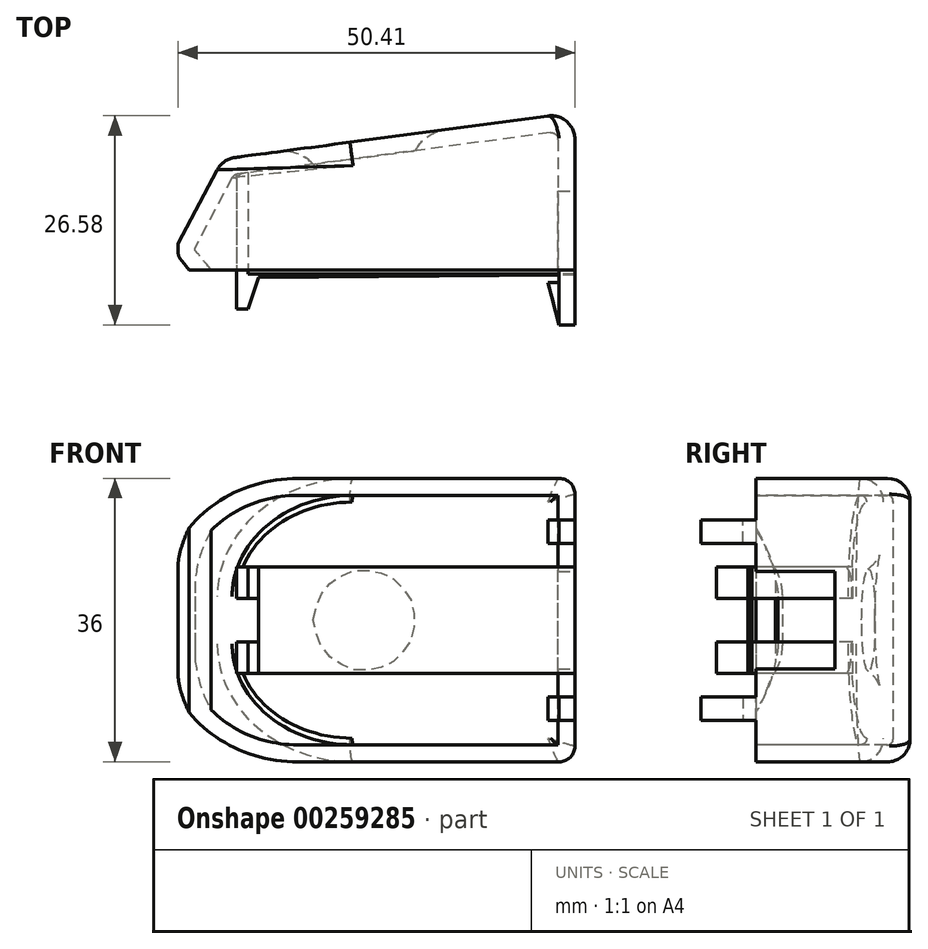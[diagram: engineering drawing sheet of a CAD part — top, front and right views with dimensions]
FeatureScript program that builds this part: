
annotation { "Feature Type Name" : "Feature", "Feature Type Description" : "" }
export const myFeature = defineFeature(function(context is Context, id is Id, definition is map)
    precondition{}
    {
        {
            var Q0;
            Q0=qCreatedBy(makeId("Top.planeOp"),FACE);
            var sketch = newSketch(context, id + "F0", { "sketchPlane" : qUnion([Q0])});
            skLineSegment(sketch, "E0.bottom", {"start": v(24.5, -10) * mm, "end": v(-24.5, -10) * mm});
            skLineSegment(sketch, "E0.left", {"start": v(24.5, -10) * mm, "end": v(24.5, 10) * mm});
            skPoint(sketch, "E0.middle", {"position": v(0, 0) * mm});
            skLineSegment(sketch, "E1", {"start": v(-20.22, 4.07) * mm, "end": v(24.5, 10) * mm});
            skLineSegment(sketch, "E2", {"start": v(-24.5, -10) * mm, "end": v(-25.9, -8.28) * mm});
            skLineSegment(sketch, "E3", {"start": v(-25.9, -8.28) * mm, "end": v(-25.9, -6.67) * mm});
            skLineSegment(sketch, "E4", {"start": v(-25.9, -6.67) * mm, "end": v(-20.22, 4.07) * mm});
            skSolve(sketch);
        }
        {
            var Q0;
            Q0=makeQuery(id+"F0.imprint","IMPRINT",FACE,{"disambiguationData":[TD([[makeQuery(id+"F0.imprint","IMPRINT",EDGE,{"derivedFrom":sQuery(id+"F0.wireOp",EDGE,"E0.bottom")}),-1.0]])]});
            var sketch = newSketch(context, id + "F1", { "sketchPlane" : qUnion([Q0])});
            skSolve(sketch);
        }
        {
            var Q0;
            Q0 = qSketchRegion(id + "F1", true);
            var Q1;
            Q1=makeQuery(id+"F0.imprint","IMPRINT",FACE,{"disambiguationData":[TD([[makeQuery(id+"F0.imprint","IMPRINT",EDGE,{"derivedFrom":sQuery(id+"F0.wireOp",EDGE,"E0.bottom")}),-1.0]])]});
            extrude(context, id + "F2", {"entities" : qUnion([Q0, Q1]), "depth" : 36 * mm});
        }
        {
            var Q0;
            Q0=makeQuery(id+"F2.opExtrude","CAP_EDGE",EDGE,{"disambiguationData":[OSD([sQuery(id+"F0.wireOp",EDGE,"E4")])],"isStart":false});
            var Q1;
            Q1=makeQuery(id+"F2.opExtrude","CAP_EDGE",EDGE,{"disambiguationData":[OSD([sQuery(id+"F0.wireOp",EDGE,"E4")])],"isStart":true});
            fillet(context, id + "F3", {"entities" : qUnion([Q0, Q1]), "radius" : 15 * mm, "tangentPropagation" : true, "allowEdgeOverflow" : false});
        }
        {
            var Q0;
            Q0=makeQuery(id+"F2.opExtrude","SWEPT_FACE",FACE,{"disambiguationData":[OSD([sQuery(id+"F0.wireOp",EDGE,"E1")])]});
            fillet(context, id + "F4", {"entities" : qUnion([Q0]), "radius" : 3 * mm, "tangentPropagation" : true, "allowEdgeOverflow" : false});
        }
        {
            var Q0;
            Q0=makeQuery(id+"F2.opExtrude","CAP_EDGE",EDGE,{"disambiguationData":[OSD([sQuery(id+"F0.wireOp",EDGE,"E0.left")])],"isStart":false});
            var Q1;
            Q1=makeQuery(id+"F2.opExtrude","CAP_EDGE",EDGE,{"disambiguationData":[OSD([sQuery(id+"F0.wireOp",EDGE,"E0.left")])],"isStart":true});
            fillet(context, id + "F5", {"entities" : qUnion([Q0, Q1]), "radius" : 2 * mm, "tangentPropagation" : true, "allowEdgeOverflow" : false});
        }
        {
            var Q0;
            Q0=makeQuery(id+"F2.opExtrude","SWEPT_FACE",FACE,{"disambiguationData":[OSD([sQuery(id+"F0.wireOp",EDGE,"E0.bottom")])]});
            var sketch = newSketch(context, id + "F6", { "sketchPlane" : qUnion([Q0])});
            skLineSegment(sketch, "E5", {"start": v(24.5, 30.74) * mm, "end": v(24.5, 27.74) * mm});
            skLineSegment(sketch, "E6.0", {"start": v(-17, 24.75) * mm, "end": v(-17, 20.75) * mm});
            skLineSegment(sketch, "E7.0", {"start": v(-18.5, 11.25) * mm, "end": v(-17, 11.25) * mm});
            skLineSegment(sketch, "E8.0", {"start": v(-18.5, 15.25) * mm, "end": v(-17, 15.25) * mm});
            skPoint(sketch, "E9.orphan", {"position": v(-17, 2) * mm});
            skPoint(sketch, "E10.orphan", {"position": v(-18.5, 2) * mm});
            skLineSegment(sketch, "E11", {"start": v(-18.5, 15.25) * mm, "end": v(-18.5, 11.25) * mm});
            skLineSegment(sketch, "E12.trimOffspring", {"start": v(-17, 15.25) * mm, "end": v(-17, 11.25) * mm});
            skLineSegment(sketch, "E13.MirrorCS", {"start": v(-18.5, 20.75) * mm, "end": v(-17, 20.75) * mm});
            skLineSegment(sketch, "E14.MirrorCS", {"start": v(-18.5, 20.75) * mm, "end": v(-18.5, 24.75) * mm});
            skLineSegment(sketch, "E15.MirrorCS", {"start": v(-18.5, 24.75) * mm, "end": v(-17, 24.75) * mm});
            skPoint(sketch, "E16.orphan", {"position": v(-17, 34) * mm});
            skLineSegment(sketch, "E17", {"start": v(22.5, 36) * mm, "end": v(31.56, 36) * mm, "construction": true});
            skLineSegment(sketch, "E18.0", {"start": v(22.5, 30.74) * mm, "end": v(24.5, 30.74) * mm});
            skLineSegment(sketch, "E19.0", {"start": v(22.5, 27.74) * mm, "end": v(24.5, 27.74) * mm});
            skLineSegment(sketch, "E20.0", {"start": v(22.5, 30.74) * mm, "end": v(22.5, 27.74) * mm});
            skLineSegment(sketch, "E21", {"start": v(24.5, 18) * mm, "end": v(40.76, 18) * mm, "construction": true});
            skLineSegment(sketch, "E22.MirrorCS", {"start": v(22.5, 8.26) * mm, "end": v(24.5, 8.26) * mm});
            skLineSegment(sketch, "E23.MirrorCS", {"start": v(22.5, 5.26) * mm, "end": v(24.5, 5.26) * mm});
            skLineSegment(sketch, "E24.MirrorCS", {"start": v(22.5, 5.26) * mm, "end": v(22.5, 8.26) * mm});
            skLineSegment(sketch, "E25.trimOffspring", {"start": v(24.5, 8.26) * mm, "end": v(24.5, 5.26) * mm});
            skPoint(sketch, "E26.orphan", {"position": v(24.5, 34) * mm});
            skPoint(sketch, "E27.orphan", {"position": v(24.5, 2) * mm});
            skLineSegment(sketch, "E28", {"start": v(24.5, 18) * mm, "end": v(-2.25, 18) * mm, "construction": true});
            skCircle(sketch, "E29", {"center": v(-2.25, 18) * mm, "radius": 6.5 * mm});
            skSolve(sketch);
        }
        {
            var Q0;
            Q0=makeQuery(id+"F2.opExtrude","SWEPT_FACE",FACE,{"disambiguationData":[OSD([sQuery(id+"F0.wireOp",EDGE,"E0.bottom")])]});
            shell(context, id + "F7", {"entities" : qUnion([Q0]), "thickness" : 2.15 * mm});
        }
        {
            var Q0;
            Q0=makeQuery(id+"F6.imprint","IMPRINT",FACE,{"disambiguationData":[TD([[makeQuery(id+"F6.imprint","IMPRINT",EDGE,{"derivedFrom":sQuery(id+"F6.wireOp",EDGE,"E5")}),-1.0]])]});
            var Q1;
            Q1=makeQuery(id+"F6.imprint","IMPRINT",FACE,{"disambiguationData":[TD([[makeQuery(id+"F6.imprint","IMPRINT",EDGE,{"derivedFrom":sQuery(id+"F6.wireOp",EDGE,"E22.MirrorCS")}),-1.0]])]});
            extrude(context, id + "F8", {"entities" : qUnion([Q0, Q1]), "operationType" : NewBodyOperationType.ADD, "depth" : 7 * mm});
        }
        {
            var Q0;
            Q0=makeQuery(id+"F6.imprint","IMPRINT",FACE,{"disambiguationData":[TD([[makeQuery(id+"F6.imprint","IMPRINT",EDGE,{"derivedFrom":sQuery(id+"F6.wireOp",EDGE,"E6.0")}),-1.0]])]});
            var Q1;
            Q1=makeQuery(id+"F6.imprint","IMPRINT",FACE,{"disambiguationData":[TD([[makeQuery(id+"F6.imprint","IMPRINT",EDGE,{"derivedFrom":sQuery(id+"F6.wireOp",EDGE,"E7.0")}),1.0]])]});
            extrude(context, id + "F9", {"entities" : qUnion([Q0, Q1]), "operationType" : NewBodyOperationType.ADD, "oppositeDirection" : true, "depth" : 14.2 * mm});
        }
        {
            var Q0;
            Q0=makeQuery(id+"F2.opExtrude","SWEPT_EDGE",EDGE,{"disambiguationData":[OSD([sQuery(id+"F0.wireOp",EDGE,"E2"),sQuery(id+"F0.wireOp",EDGE,"E3")])]});
            fillet(context, id + "F10", {"entities" : qUnion([Q0]), "radius" : 1.62 * mm, "tangentPropagation" : true, "allowEdgeOverflow" : false});
        }
        {
            var Q0;
            Q0=makeQuery(id+"F6.imprint","IMPRINT",FACE,{"disambiguationData":[TD([[makeQuery(id+"F6.imprint","IMPRINT",EDGE,{"derivedFrom":sQuery(id+"F6.wireOp",EDGE,"E6.0")}),-1.0]])]});
            var Q1;
            Q1=makeQuery(id+"F6.imprint","IMPRINT",FACE,{"disambiguationData":[TD([[makeQuery(id+"F6.imprint","IMPRINT",EDGE,{"derivedFrom":sQuery(id+"F6.wireOp",EDGE,"E7.0")}),1.0]])]});
            extrude(context, id + "F11", {"entities" : qUnion([Q0, Q1]), "operationType" : NewBodyOperationType.ADD, "depth" : 5 * mm});
        }
        {
            var Q0;
            Q0=makeQuery(id+"F6.imprint","IMPRINT",FACE,{"disambiguationData":[TD([[makeQuery(id+"F6.imprint","IMPRINT",EDGE,{"derivedFrom":sQuery(id+"F6.wireOp",EDGE,"E29")}),1.0]])]});
            extrude(context, id + "F12", {"entities" : qUnion([Q0]), "operationType" : NewBodyOperationType.REMOVE, "oppositeDirection" : true, "depth" : 25 * mm});
        }
        {
            var Q0;
            Q0=makeQuery(id+"F12.boolean.opBoolean","INTERSECT",EDGE,{"derivedFrom":[makeQuery(id+"F2.opExtrude","SWEPT_FACE",FACE,{"disambiguationData":[OSD([sQuery(id+"F0.wireOp",EDGE,"E1")])]}),makeQuery(id+"F12.opExtrude","SWEPT_FACE",FACE,{"disambiguationData":[OSD([sQuery(id+"F6.wireOp",EDGE,"E29")])]})]});
            fillet(context, id + "F13", {"entities" : qUnion([Q0]), "radius" : 5 * mm, "tangentPropagation" : true, "allowEdgeOverflow" : false});
        }
        {
            var Q0;
            Q0=makeQuery(id+"F8.opExtrude","SWEPT_FACE",FACE,{"disambiguationData":[OSD([sQuery(id+"F6.wireOp",EDGE,"E23.MirrorCS")])]});
            var sketch = newSketch(context, id + "F14", { "sketchPlane" : qUnion([Q0])});
            skLineSegment(sketch, "E30.MirrorCS", {"start": v(22.5, 11.65) * mm, "end": v(22.5, 17) * mm});
            skLineSegment(sketch, "E31.MirrorCS", {"start": v(22.5, 17) * mm, "end": v(21.09, 11.65) * mm});
            skLineSegment(sketch, "E32.MirrorCS", {"start": v(21.09, 11.65) * mm, "end": v(22.5, 11.65) * mm});
            skSolve(sketch);
        }
        {
            var Q0;
            Q0=makeQuery(id+"F8.opExtrude","SWEPT_FACE",FACE,{"disambiguationData":[OSD([sQuery(id+"F6.wireOp",EDGE,"E18.0")])]});
            var sketch = newSketch(context, id + "F15", { "sketchPlane" : qUnion([Q0])});
            skLineSegment(sketch, "E33.MirrorCS", {"start": v(22.5, -17) * mm, "end": v(22.5, -11.63) * mm});
            skLineSegment(sketch, "E34.MirrorCS", {"start": v(21.09, -11.63) * mm, "end": v(22.5, -17) * mm});
            skLineSegment(sketch, "E35.MirrorCS", {"start": v(22.5, -11.63) * mm, "end": v(21.09, -11.63) * mm});
            skSolve(sketch);
        }
        {
            var Q0;
            {var subQ0=sQuery(id+"F14.wireOp",EDGE,"E32.MirrorCS");var subQ1=sQuery(id+"F14.wireOp",EDGE,"E31.MirrorCS");var subQ2=makeQuery(id+"F14.imprint","INTERSECT",VERTEX,{"derivedFrom":[subQ1,subQ0]});Q0=makeQuery(id+"F14.imprint","IMPRINT",FACE,{"disambiguationData":[TD([[makeQuery(id+"F14.imprint","IMPRINT",EDGE,{"disambiguationData":[TD([[subQ2,1.0]])],"derivedFrom":subQ1}),1.0]])]});}
            extrude(context, id + "F16", {"entities" : qUnion([Q0]), "operationType" : NewBodyOperationType.ADD, "oppositeDirection" : true, "depth" : 3 * mm});
        }
        {
            var Q0;
            Q0=makeQuery(id+"F15.imprint","IMPRINT",FACE,{"disambiguationData":[TD([[makeQuery(id+"F15.imprint","IMPRINT",EDGE,{"derivedFrom":sQuery(id+"F15.wireOp",EDGE,"E33.MirrorCS")}),1.0]])]});
            extrude(context, id + "F17", {"entities" : qUnion([Q0]), "oppositeDirection" : true, "depth" : 3 * mm});
        }
        {
            var Q0;
            {var subQ0=sQuery(id+"F6.wireOp",EDGE,"E15.MirrorCS");var subQ1=sQuery(id+"F6.wireOp",EDGE,"E6.0");Q0=makeQuery(id+"F11.boolean.opBoolean","MERGE",FACE,{"derivedFrom":[makeQuery(id+"F9.boolean.opBoolean","SPLIT",FACE,{"disambiguationData":[TD([makeQuery(id+"F9.opExtrude","SWEPT_FACE",FACE,{"disambiguationData":[OSD([subQ1])]})])],"derivedFrom":makeQuery(id+"F9.opExtrude","SWEPT_FACE",FACE,{"disambiguationData":[OSD([subQ0])]})}),makeQuery(id+"F11.opExtrude","SWEPT_FACE",FACE,{"disambiguationData":[OSD([subQ0])]})]});}
            var sketch = newSketch(context, id + "F18", { "sketchPlane" : qUnion([Q0])});
            skLineSegment(sketch, "E36", {"start": v(-18.5, -15) * mm, "end": v(-17, -15) * mm});
            skLineSegment(sketch, "E37", {"start": v(-17, -15) * mm, "end": v(-15.54, -10.53) * mm});
            skLineSegment(sketch, "E38", {"start": v(-15.54, -10.53) * mm, "end": v(-17, -10.53) * mm});
            skLineSegment(sketch, "E39", {"start": v(-17, -10.53) * mm, "end": v(-17, -15) * mm});
            skSolve(sketch);
        }
        {
            var Q0;
            Q0=makeQuery(id+"F18.imprint","IMPRINT",FACE,{"disambiguationData":[TD([[makeQuery(id+"F18.imprint","IMPRINT",EDGE,{"derivedFrom":sQuery(id+"F18.wireOp",EDGE,"E37")}),1.0]])]});
            extrude(context, id + "F19", {"entities" : qUnion([Q0]), "operationType" : NewBodyOperationType.ADD, "oppositeDirection" : true, "depth" : 4 * mm});
        }
        {
            var Q0;
            {var subQ0=sQuery(id+"F6.wireOp",EDGE,"E7.0");var subQ1=sQuery(id+"F6.wireOp",EDGE,"E12.trimOffspring");Q0=makeQuery(id+"F11.boolean.opBoolean","MERGE",FACE,{"derivedFrom":[makeQuery(id+"F9.boolean.opBoolean","SPLIT",FACE,{"disambiguationData":[TD([makeQuery(id+"F9.opExtrude","SWEPT_FACE",FACE,{"disambiguationData":[OSD([subQ1])]})])],"derivedFrom":makeQuery(id+"F9.opExtrude","SWEPT_FACE",FACE,{"disambiguationData":[OSD([subQ0])]})}),makeQuery(id+"F11.opExtrude","SWEPT_FACE",FACE,{"disambiguationData":[OSD([subQ0])]})]});}
            var sketch = newSketch(context, id + "F20", { "sketchPlane" : qUnion([Q0])});
            skLineSegment(sketch, "E40", {"start": v(-18.5, 15) * mm, "end": v(-17, 15) * mm});
            skLineSegment(sketch, "E41", {"start": v(-17, 15) * mm, "end": v(-15.54, 10.53) * mm});
            skLineSegment(sketch, "E42", {"start": v(-15.54, 10.53) * mm, "end": v(-17, 10.53) * mm});
            skLineSegment(sketch, "E43", {"start": v(-17, 10.53) * mm, "end": v(-17, 15) * mm});
            skSolve(sketch);
        }
        {
            var Q0;
            Q0=makeQuery(id+"F20.imprint","IMPRINT",FACE,{"disambiguationData":[TD([[makeQuery(id+"F20.imprint","IMPRINT",EDGE,{"derivedFrom":sQuery(id+"F20.wireOp",EDGE,"E41")}),-1.0]])]});
            extrude(context, id + "F21", {"entities" : qUnion([Q0]), "operationType" : NewBodyOperationType.ADD, "oppositeDirection" : true, "depth" : 4 * mm});
        }
        {
            var Q0;
            {var subQ0=sQuery(id+"F6.wireOp",EDGE,"E15.MirrorCS");var subQ1=sQuery(id+"F6.wireOp",EDGE,"E6.0");Q0=makeQuery(id+"F19.boolean.opBoolean","MERGE",FACE,{"derivedFrom":[makeQuery(id+"F11.boolean.opBoolean","MERGE",FACE,{"derivedFrom":[makeQuery(id+"F9.boolean.opBoolean","SPLIT",FACE,{"disambiguationData":[TD([makeQuery(id+"F9.opExtrude","SWEPT_FACE",FACE,{"disambiguationData":[OSD([subQ1])]})])],"derivedFrom":makeQuery(id+"F9.opExtrude","SWEPT_FACE",FACE,{"disambiguationData":[OSD([subQ0])]})}),makeQuery(id+"F11.opExtrude","SWEPT_FACE",FACE,{"disambiguationData":[OSD([subQ0])]})]}),makeQuery(id+"F19.opExtrude","CAP_FACE",FACE,{"disambiguationData":[OSD([sQuery(id+"F18.wireOp",EDGE,"E37"),sQuery(id+"F18.wireOp",EDGE,"E38"),sQuery(id+"F18.wireOp",EDGE,"E39")])],"isStart":true})]});}
            var sketch = newSketch(context, id + "F22", { "sketchPlane" : qUnion([Q0])});
            skLineSegment(sketch, "E44", {"start": v(-15.54, -10.53) * mm, "end": v(24.5, -10.53) * mm});
            skLineSegment(sketch, "E45", {"start": v(24.5, -10.53) * mm, "end": v(24.5, -10.63) * mm});
            skLineSegment(sketch, "E46", {"start": v(24.5, -10.63) * mm, "end": v(-15.69, -11) * mm});
            skLineSegment(sketch, "E47", {"start": v(-15.69, -11) * mm, "end": v(-15.54, -10.53) * mm});
            skSolve(sketch);
        }
        {
            var Q0;
            Q0=makeQuery(id+"F22.imprint","IMPRINT",FACE,{"disambiguationData":[TD([[makeQuery(id+"F22.imprint","IMPRINT",EDGE,{"derivedFrom":sQuery(id+"F22.wireOp",EDGE,"E44")}),-1.0]])]});
            extrude(context, id + "F23", {"entities" : qUnion([Q0]), "operationType" : NewBodyOperationType.ADD, "oppositeDirection" : true, "depth" : 13.5 * mm});
        }
        {
            var Q0;
            Q0=makeQuery(id+"F8.boolean.opBoolean","MERGE",FACE,{"derivedFrom":[makeQuery(id+"F2.opExtrude","SWEPT_FACE",FACE,{"disambiguationData":[OSD([sQuery(id+"F0.wireOp",EDGE,"E0.left")])]}),makeQuery(id+"F8.opExtrude","SWEPT_FACE",FACE,{"disambiguationData":[OSD([sQuery(id+"F6.wireOp",EDGE,"E5")])]}),makeQuery(id+"F8.opExtrude","SWEPT_FACE",FACE,{"disambiguationData":[OSD([sQuery(id+"F6.wireOp",EDGE,"E25.trimOffspring")])]})]});
            var sketch = newSketch(context, id + "F24", { "sketchPlane" : qUnion([Q0])});
            skLineSegment(sketch, "E48.bottom", {"start": v(0, 24.2) * mm, "end": v(-20, 24.2) * mm});
            skLineSegment(sketch, "E48.top", {"start": v(0, 11.8) * mm, "end": v(-20, 11.8) * mm});
            skLineSegment(sketch, "E48.left", {"start": v(0, 24.2) * mm, "end": v(0, 11.8) * mm});
            skLineSegment(sketch, "E48.right", {"start": v(-20, 24.2) * mm, "end": v(-20, 11.8) * mm});
            skPoint(sketch, "E48.middle", {"position": v(-10, 18) * mm});
            skSolve(sketch);
        }
        {
            var Q0;
            {var subQ0=sQuery(id+"F24.wireOp",EDGE,"E48.left");Q0=makeQuery(id+"F24.imprint","IMPRINT",FACE,{"disambiguationData":[TD([[makeQuery(id+"F24.imprint","IMPRINT",EDGE,{"derivedFrom":subQ0}),-1.0]])]});}
            extrude(context, id + "F25", {"entities" : qUnion([Q0]), "operationType" : NewBodyOperationType.REMOVE, "oppositeDirection" : true, "depth" : 3 * mm});
        }
    });
